# Revit family: Bowl-Toilet-American_Standard-Cadet-3517A.101.020
name_source: partatom
category: Plumbing Fixtures
revit_build: Autodesk Revit 2015 (Build: 20140606_1530(x64)
units: mm (PartAtom-declared; Revit-internal decimal feet)

## types (14) — shared parameters
ADA Compliant = Yes
Assembly Code = D2010110
Bowl Shape = Elongated
CW Connection = Yes
CWFU = 5
Cold Water Connection Diameter = 1/2"
Cold Water Connection Height = 10"
Cold Water Connection Radius = 1/4"
Cold Water Connection Width = 6"
Default Elevation = 0"
HW Connection = No
Height = 30 3/8"
Installation Type = Floor Mounted
Length = 30 1/8"
Manufacturer = American Standard
Price = Prices may vary. Please consult Manufacturer Representative for most up-to-date price list.
Product Documentation Link = https://www.americanstandard-us.com
Product Page URL = https://www.americanstandard-us.com
Revised Date = 01/14/2019
Shipping Weight = 80lb (40.7kg)
URL = http://www.americanstandard-us.com
Vent Connection = No
WFU = 5
Warranty Information = 5 Years Limited
Waste Connection = Yes
Waste Connection Diameter = 2 1/8"
Waste Connection Radius = 1 1/16"
Width = 17 3/8"
zero-valued in all types: HWFU

## per-type parameters (varying)
| type | Aquaguard Liner | Description | Finish | Flush Rate | Left Trip Lever | Material | Right Trip Lever | Type Comments |
| 215AA.104.020 | No | Cadet PRO Right Height Elongated 1.28 gpf Toilet | Vitreous China-American Standard-020-White | 1.28 gpf (4.8Lpf) | Yes | Vitreous China-American Standard-020-White | No | Available Finishes: White, Linen, Bone and Black. |
| 215AA.154.020 | Yes | Cadet PRO Right Height Elongated 1.28 gpf Toilet | Vitreous China-American Standard-020-White | 1.28 gpf (4.8Lpf) | Yes | Vitreous China-American Standard-020-White | No | Available Finishes: White, Linen and Bone. |
| 215AA 004.020 | No | Cadet PRO Right Height Elongated 1.6 gpf Toilet | Vitreous China-American Standard-020-White | 1.6 gpf (6.0Lpf) | Yes | Vitreous China-American Standard-020-White | No | Available Finishes: White, Linen, Bone and Black. |
| 215AA 004.021 | No | Cadet PRO Right Height Elongated 1.6 gpf Toilet | Vitreous China-American Standard-021-Bone | 1.6 gpf (6.0Lpf) | Yes | Vitreous China-American Standard-021-Bone | No | Available Finishes: White, Linen, Bone and Black. |
| 215AA 004.222 | No | Cadet PRO Right Height Elongated 1.6 gpf Toilet | Vitreous China-American Standard-222-Linen | 1.6 gpf (6.0Lpf) | Yes | Vitreous China-American Standard-222-Linen | No | Available Finishes: White, Linen, Bone and Black. |
| 215AA.005.020 | No | Cadet PRO Right Height Elongated 1.6 gpf Toilet | Vitreous China-American Standard-020-White | 1.6 gpf (6.0Lpf) | No | Vitreous China-American Standard-020-White | Yes | Available Finishes: White, Linen, Bone and Black. |
| 215AA.104.021 | No | Cadet PRO Right Height Elongated 1.28 gpf Toilet | Vitreous China-American Standard-021-Bone | 1.28 gpf (4.8Lpf) | Yes | Vitreous China-American Standard-021-Bone | No | Available Finishes: White, Linen, Bone and Black. |
| 215AA.104.222 | No | Cadet PRO Right Height Elongated 1.28 gpf Toilet | Vitreous China-American Standard-222-Linen | 1.28 gpf (4.8Lpf) | Yes | Vitreous China-American Standard-222-Linen | No | Available Finishes: White, Linen, Bone and Black. |
| 215AA.105.020 | No | Cadet PRO Right Height Elongated 1.28 gpf Toilet | Vitreous China-American Standard-020-White | 1.28 gpf (4.8Lpf) | No | Vitreous China-American Standard-020-White | Yes | Available Finishes: White, Linen, Bone and Black. |
| 215AA.154.021 | Yes | Cadet PRO Right Height Elongated 1.28 gpf Toilet | Vitreous China-American Standard-021-Bone | 1.28 gpf (4.8Lpf) | Yes | Vitreous China-American Standard-021-Bone | No | Available Finishes: White, Linen and Bone. |
| 215AA.154.222 | Yes | Cadet PRO Right Height Elongated 1.28 gpf Toilet | Vitreous China-American Standard-222-Linen | 1.28 gpf (4.8Lpf) | Yes | Vitreous China-American Standard-222-Linen | No | Available Finishes: White, Linen and Bone. |
| 215AA 054.020 | Yes | Cadet PRO Right Height Elongated 1.6 gpf Toilet | Vitreous China-American Standard-020-White | 1.6 gpf (6.0Lpf) | Yes | Vitreous China-American Standard-020-White | No | Available Finishes: White, Linen, Bone and Black. |
| 215AA 054.021 | Yes | Cadet PRO Right Height Elongated 1.6 gpf Toilet | Vitreous China-American Standard-021-Bone | 1.6 gpf (6.0Lpf) | Yes | Vitreous China-American Standard-021-Bone | No | Available Finishes: White, Linen, Bone and Black. |
| 215AA 054.222 | Yes | Cadet PRO Right Height Elongated 1.6 gpf Toilet | Vitreous China-American Standard-222-Linen | 1.6 gpf (6.0Lpf) | Yes | Vitreous China-American Standard-222-Linen | No | Available Finishes: White, Linen, Bone and Black. |

note: column(s) folded — value = type name in every type: Model

## geometry (parser evidence)
native form markers: Sweep x3
no freeform markers — native parametric forms only
